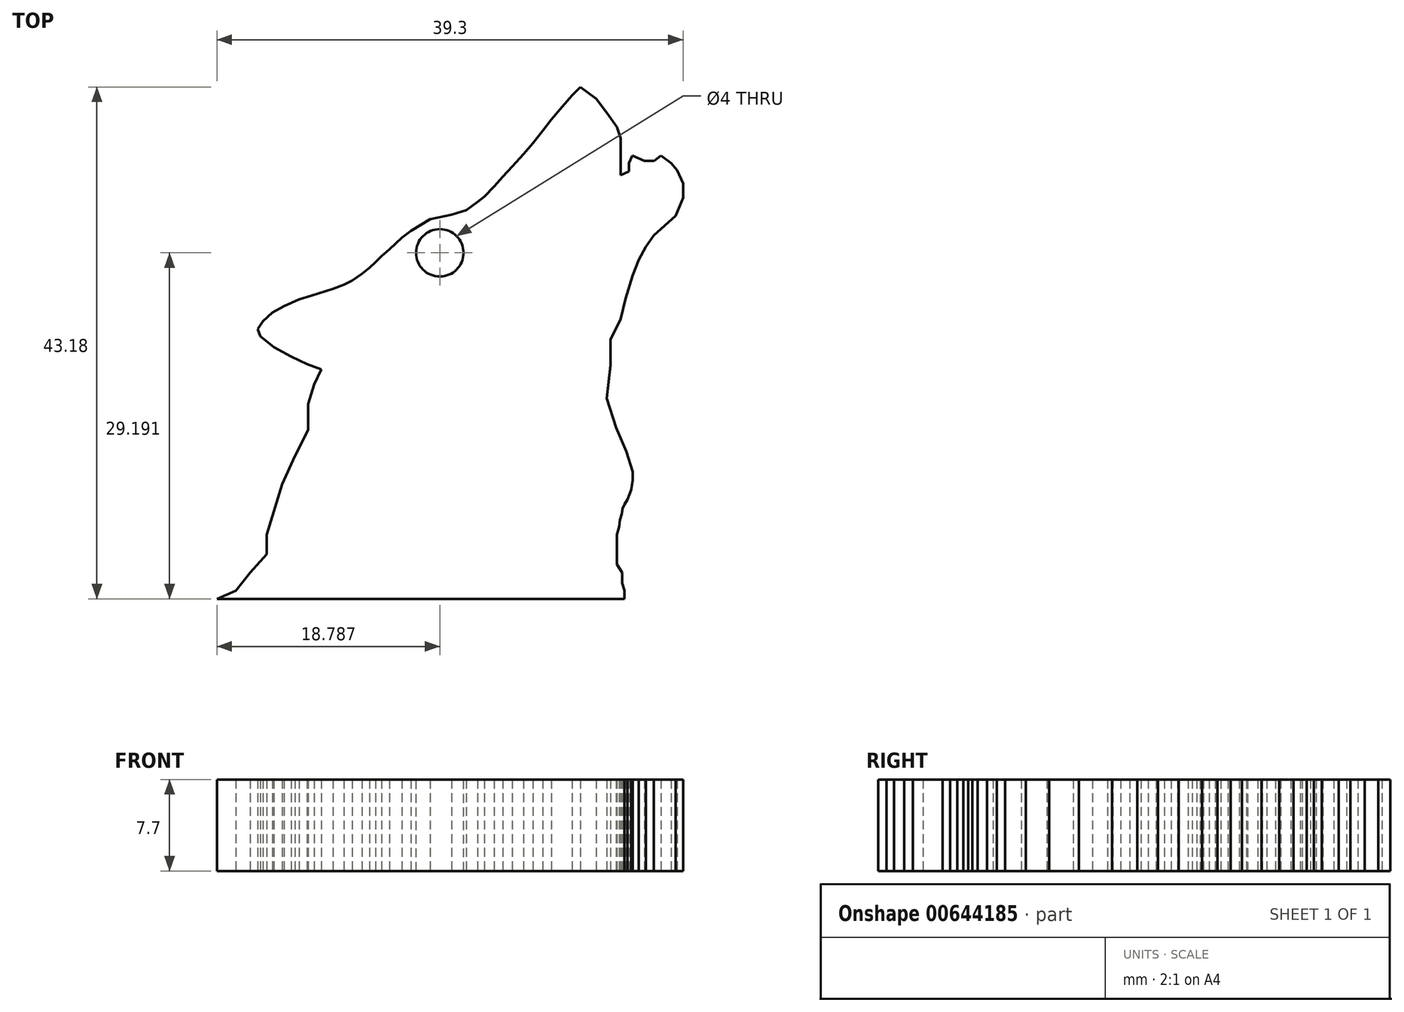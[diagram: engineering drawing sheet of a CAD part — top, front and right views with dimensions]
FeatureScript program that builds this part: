
annotation { "Feature Type Name" : "Feature", "Feature Type Description" : "" }
export const myFeature = defineFeature(function(context is Context, id is Id, definition is map)
    precondition{}
    {
        {
            var Q0;
            Q0=qCreatedBy(makeId("Top.planeOp"),FACE);
            var sketch = newSketch(context, id + "F0", { "sketchPlane" : qUnion([Q0])});
            skLineSegment(sketch, "E0", {"start": v(-37.66, 39.45) * mm, "end": v(-38.87, 39.9) * mm});
            skLineSegment(sketch, "E1", {"start": v(-38.87, 39.9) * mm, "end": v(-40.2, 40.55) * mm});
            skLineSegment(sketch, "E2", {"start": v(-40.2, 40.55) * mm, "end": v(-41.64, 41.33) * mm});
            skLineSegment(sketch, "E3", {"start": v(-41.64, 41.33) * mm, "end": v(-42.8, 42.26) * mm});
            skLineSegment(sketch, "E4", {"start": v(-42.8, 42.26) * mm, "end": v(-43.02, 42.87) * mm});
            skLineSegment(sketch, "E5", {"start": v(-43.02, 42.87) * mm, "end": v(-42.58, 43.53) * mm});
            skLineSegment(sketch, "E6", {"start": v(-42.58, 43.53) * mm, "end": v(-41.77, 44.24) * mm});
            skLineSegment(sketch, "E7", {"start": v(-41.77, 44.24) * mm, "end": v(-40.79, 44.8) * mm});
            skLineSegment(sketch, "E8", {"start": v(-40.79, 44.8) * mm, "end": v(-39.53, 45.35) * mm});
            skLineSegment(sketch, "E9", {"start": v(-39.53, 45.35) * mm, "end": v(-38.46, 45.68) * mm});
            skLineSegment(sketch, "E10", {"start": v(-38.46, 45.68) * mm, "end": v(-36.68, 46.24) * mm});
            skLineSegment(sketch, "E11", {"start": v(-36.68, 46.24) * mm, "end": v(-35.74, 46.6) * mm});
            skLineSegment(sketch, "E12", {"start": v(-35.74, 46.6) * mm, "end": v(-35.04, 46.96) * mm});
            skLineSegment(sketch, "E13", {"start": v(-35.04, 46.96) * mm, "end": v(-34.22, 47.52) * mm});
            skLineSegment(sketch, "E14", {"start": v(-34.22, 47.52) * mm, "end": v(-33.6, 48.02) * mm});
            skLineSegment(sketch, "E15", {"start": v(-33.6, 48.02) * mm, "end": v(-33.08, 48.52) * mm});
            skLineSegment(sketch, "E16", {"start": v(-33.08, 48.52) * mm, "end": v(-32.58, 49.01) * mm});
            skLineSegment(sketch, "E17", {"start": v(-32.58, 49.01) * mm, "end": v(-31.92, 49.6) * mm});
            skLineSegment(sketch, "E18", {"start": v(-31.92, 49.6) * mm, "end": v(-31.4, 50.06) * mm});
            skLineSegment(sketch, "E19", {"start": v(-31.4, 50.06) * mm, "end": v(-30.86, 50.57) * mm});
            skLineSegment(sketch, "E20", {"start": v(-30.86, 50.57) * mm, "end": v(-30.1, 51.15) * mm});
            skLineSegment(sketch, "E21", {"start": v(-30.1, 51.15) * mm, "end": v(-28.46, 52.13) * mm});
            skLineSegment(sketch, "E22", {"start": v(-28.46, 52.13) * mm, "end": v(-26.65, 52.5) * mm});
            skLineSegment(sketch, "E23", {"start": v(-26.65, 52.5) * mm, "end": v(-25.42, 52.89) * mm});
            skLineSegment(sketch, "E24", {"start": v(-25.42, 52.89) * mm, "end": v(-24.47, 53.59) * mm});
            skLineSegment(sketch, "E25", {"start": v(-24.47, 53.59) * mm, "end": v(-23.9, 54.05) * mm});
            skLineSegment(sketch, "E26", {"start": v(-23.9, 54.05) * mm, "end": v(-23.08, 54.9) * mm});
            skLineSegment(sketch, "E27", {"start": v(-23.08, 54.9) * mm, "end": v(-22.33, 55.7) * mm});
            skLineSegment(sketch, "E28", {"start": v(-22.33, 55.7) * mm, "end": v(-21.57, 56.56) * mm});
            skLineSegment(sketch, "E29", {"start": v(-21.57, 56.56) * mm, "end": v(-20.59, 57.61) * mm});
            skLineSegment(sketch, "E30", {"start": v(-20.59, 57.61) * mm, "end": v(-19.8, 58.54) * mm});
            skLineSegment(sketch, "E31", {"start": v(-19.8, 58.54) * mm, "end": v(-19, 59.6) * mm});
            skLineSegment(sketch, "E32", {"start": v(-19, 59.6) * mm, "end": v(-18.25, 60.54) * mm});
            skLineSegment(sketch, "E33", {"start": v(-18.25, 60.54) * mm, "end": v(-17.32, 61.62) * mm});
            skLineSegment(sketch, "E34", {"start": v(-17.32, 61.62) * mm, "end": v(-16.5, 62.58) * mm});
            skLineSegment(sketch, "E35", {"start": v(-16.5, 62.58) * mm, "end": v(-15.8, 63.28) * mm});
            skLineSegment(sketch, "E36", {"start": v(-15.8, 63.28) * mm, "end": v(-14.5, 62.27) * mm});
            skLineSegment(sketch, "E37", {"start": v(-14.5, 62.27) * mm, "end": v(-13.58, 61.13) * mm});
            skLineSegment(sketch, "E38", {"start": v(-13.58, 61.13) * mm, "end": v(-12.71, 59.91) * mm});
            skLineSegment(sketch, "E39", {"start": v(-12.71, 59.91) * mm, "end": v(-12.41, 58.95) * mm});
            skLineSegment(sketch, "E40", {"start": v(-12.41, 58.95) * mm, "end": v(-12.41, 57.55) * mm});
            skLineSegment(sketch, "E41", {"start": v(-12.41, 57.55) * mm, "end": v(-12.41, 55.85) * mm});
            skLineSegment(sketch, "E42", {"start": v(-12.41, 55.85) * mm, "end": v(-11.7, 56.16) * mm});
            skLineSegment(sketch, "E43", {"start": v(-11.7, 56.16) * mm, "end": v(-11.7, 56.85) * mm});
            skLineSegment(sketch, "E44", {"start": v(-11.7, 56.85) * mm, "end": v(-11.43, 57.48) * mm});
            skLineSegment(sketch, "E45", {"start": v(-11.43, 57.48) * mm, "end": v(-10.42, 57.05) * mm});
            skLineSegment(sketch, "E46", {"start": v(-10.42, 57.05) * mm, "end": v(-9.58, 57.05) * mm});
            skLineSegment(sketch, "E47", {"start": v(-9.58, 57.05) * mm, "end": v(-9.02, 57.5) * mm});
            skLineSegment(sketch, "E48", {"start": v(-9.02, 57.5) * mm, "end": v(-8.16, 56.85) * mm});
            skLineSegment(sketch, "E49", {"start": v(-8.16, 56.85) * mm, "end": v(-7.64, 56.25) * mm});
            skLineSegment(sketch, "E50", {"start": v(-7.64, 56.25) * mm, "end": v(-7.15, 55.14) * mm});
            skLineSegment(sketch, "E51", {"start": v(-7.15, 55.14) * mm, "end": v(-7.15, 53.93) * mm});
            skLineSegment(sketch, "E52", {"start": v(-7.15, 53.93) * mm, "end": v(-7.76, 52.41) * mm});
            skLineSegment(sketch, "E53", {"start": v(-7.76, 52.41) * mm, "end": v(-9.63, 50.78) * mm});
            skLineSegment(sketch, "E54", {"start": v(-9.63, 50.78) * mm, "end": v(-10.28, 49.83) * mm});
            skLineSegment(sketch, "E55", {"start": v(-10.28, 49.83) * mm, "end": v(-10.87, 48.71) * mm});
            skLineSegment(sketch, "E56", {"start": v(-10.87, 48.71) * mm, "end": v(-11.4, 47.4) * mm});
            skLineSegment(sketch, "E57", {"start": v(-11.4, 47.4) * mm, "end": v(-11.99, 45.44) * mm});
            skLineSegment(sketch, "E58", {"start": v(-11.99, 45.44) * mm, "end": v(-12.41, 43.71) * mm});
            skLineSegment(sketch, "E59", {"start": v(-12.41, 43.71) * mm, "end": v(-13.28, 41.95) * mm});
            skLineSegment(sketch, "E60", {"start": v(-13.28, 41.95) * mm, "end": v(-13.28, 39.82) * mm});
            skLineSegment(sketch, "E61", {"start": v(-13.28, 39.82) * mm, "end": v(-13.58, 37.03) * mm});
            skLineSegment(sketch, "E62", {"start": v(-13.58, 37.03) * mm, "end": v(-13.28, 36.06) * mm});
            skLineSegment(sketch, "E63", {"start": v(-13.28, 36.06) * mm, "end": v(-12.8, 34.53) * mm});
            skLineSegment(sketch, "E64", {"start": v(-12.8, 34.53) * mm, "end": v(-11.93, 32.55) * mm});
            skLineSegment(sketch, "E65", {"start": v(-11.93, 32.55) * mm, "end": v(-11.38, 30.81) * mm});
            skLineSegment(sketch, "E66", {"start": v(-11.38, 30.81) * mm, "end": v(-11.38, 30.12) * mm});
            skLineSegment(sketch, "E67", {"start": v(-11.38, 30.12) * mm, "end": v(-11.53, 29.3) * mm});
            skLineSegment(sketch, "E68", {"start": v(-11.53, 29.3) * mm, "end": v(-11.85, 28.48) * mm});
            skLineSegment(sketch, "E69", {"start": v(-11.85, 28.48) * mm, "end": v(-12.09, 28.06) * mm});
            skLineSegment(sketch, "E70", {"start": v(-12.09, 28.06) * mm, "end": v(-12.25, 27.7) * mm});
            skLineSegment(sketch, "E71", {"start": v(-12.25, 27.7) * mm, "end": v(-12.32, 27.28) * mm});
            skLineSegment(sketch, "E72", {"start": v(-12.32, 27.28) * mm, "end": v(-12.48, 26.77) * mm});
            skLineSegment(sketch, "E73", {"start": v(-12.48, 26.77) * mm, "end": v(-12.53, 26.18) * mm});
            skLineSegment(sketch, "E74", {"start": v(-12.53, 26.18) * mm, "end": v(-12.73, 25.52) * mm});
            skLineSegment(sketch, "E75", {"start": v(-12.73, 25.52) * mm, "end": v(-12.73, 24.66) * mm});
            skLineSegment(sketch, "E76", {"start": v(-12.73, 24.66) * mm, "end": v(-12.73, 23.8) * mm});
            skLineSegment(sketch, "E77", {"start": v(-12.73, 23.8) * mm, "end": v(-12.73, 23.01) * mm});
            skLineSegment(sketch, "E78", {"start": v(-12.73, 23.01) * mm, "end": v(-12.29, 22.3) * mm});
            skLineSegment(sketch, "E79", {"start": v(-12.29, 22.3) * mm, "end": v(-12.29, 21.44) * mm});
            skLineSegment(sketch, "E80", {"start": v(-12.29, 21.44) * mm, "end": v(-12.09, 20.8) * mm});
            skLineSegment(sketch, "E81", {"start": v(-12.09, 20.8) * mm, "end": v(-12.09, 20.1) * mm});
            skLineSegment(sketch, "E82", {"start": v(-12.09, 20.1) * mm, "end": v(-46.45, 20.1) * mm});
            skLineSegment(sketch, "E83", {"start": v(-46.45, 20.1) * mm, "end": v(-44.87, 20.8) * mm});
            skLineSegment(sketch, "E84", {"start": v(-44.87, 20.8) * mm, "end": v(-43.66, 22.3) * mm});
            skLineSegment(sketch, "E85", {"start": v(-43.66, 22.3) * mm, "end": v(-42.25, 23.88) * mm});
            skLineSegment(sketch, "E86", {"start": v(-42.25, 23.88) * mm, "end": v(-42.25, 25.5) * mm});
            skLineSegment(sketch, "E87", {"start": v(-42.25, 25.5) * mm, "end": v(-41.67, 27.4) * mm});
            skLineSegment(sketch, "E88", {"start": v(-41.67, 27.4) * mm, "end": v(-40.95, 29.79) * mm});
            skLineSegment(sketch, "E89", {"start": v(-40.95, 29.79) * mm, "end": v(-39.87, 32.17) * mm});
            skLineSegment(sketch, "E90", {"start": v(-39.87, 32.17) * mm, "end": v(-38.75, 34.33) * mm});
            skLineSegment(sketch, "E91", {"start": v(-38.75, 34.33) * mm, "end": v(-38.75, 36.54) * mm});
            skLineSegment(sketch, "E92", {"start": v(-38.75, 36.54) * mm, "end": v(-38.25, 38.19) * mm});
            skLineSegment(sketch, "E93", {"start": v(-38.25, 38.19) * mm, "end": v(-37.66, 39.45) * mm});
            skSolve(sketch);
        }
        {
            var Q0;
            Q0 = qSketchRegion(id + "F0", true);
            extrude(context, id + "F1", {"entities" : qUnion([Q0]), "depth" : 7.7 * mm, "offsetDistance" : 25.4 * mm});
        }
        {
            var Q0;
            Q0=makeQuery(id+"F1.opExtrude","CAP_FACE",FACE,{"disambiguationData":[OSD([sQuery(id+"F0.wireOp",EDGE,"E0"),sQuery(id+"F0.wireOp",EDGE,"E1"),sQuery(id+"F0.wireOp",EDGE,"E2"),sQuery(id+"F0.wireOp",EDGE,"E3"),sQuery(id+"F0.wireOp",EDGE,"E4"),sQuery(id+"F0.wireOp",EDGE,"E5"),sQuery(id+"F0.wireOp",EDGE,"E6"),sQuery(id+"F0.wireOp",EDGE,"E7"),sQuery(id+"F0.wireOp",EDGE,"E8"),sQuery(id+"F0.wireOp",EDGE,"E9"),sQuery(id+"F0.wireOp",EDGE,"E10"),sQuery(id+"F0.wireOp",EDGE,"E11"),sQuery(id+"F0.wireOp",EDGE,"E12"),sQuery(id+"F0.wireOp",EDGE,"E13"),sQuery(id+"F0.wireOp",EDGE,"E14"),sQuery(id+"F0.wireOp",EDGE,"E15"),sQuery(id+"F0.wireOp",EDGE,"E16"),sQuery(id+"F0.wireOp",EDGE,"E17"),sQuery(id+"F0.wireOp",EDGE,"E18"),sQuery(id+"F0.wireOp",EDGE,"E19"),sQuery(id+"F0.wireOp",EDGE,"E20"),sQuery(id+"F0.wireOp",EDGE,"E21"),sQuery(id+"F0.wireOp",EDGE,"E22"),sQuery(id+"F0.wireOp",EDGE,"E23"),sQuery(id+"F0.wireOp",EDGE,"E24"),sQuery(id+"F0.wireOp",EDGE,"E25"),sQuery(id+"F0.wireOp",EDGE,"E26"),sQuery(id+"F0.wireOp",EDGE,"E27"),sQuery(id+"F0.wireOp",EDGE,"E28"),sQuery(id+"F0.wireOp",EDGE,"E29"),sQuery(id+"F0.wireOp",EDGE,"E30"),sQuery(id+"F0.wireOp",EDGE,"E31"),sQuery(id+"F0.wireOp",EDGE,"E32"),sQuery(id+"F0.wireOp",EDGE,"E33"),sQuery(id+"F0.wireOp",EDGE,"E34"),sQuery(id+"F0.wireOp",EDGE,"E35"),sQuery(id+"F0.wireOp",EDGE,"E36"),sQuery(id+"F0.wireOp",EDGE,"E37"),sQuery(id+"F0.wireOp",EDGE,"E38"),sQuery(id+"F0.wireOp",EDGE,"E39"),sQuery(id+"F0.wireOp",EDGE,"E40"),sQuery(id+"F0.wireOp",EDGE,"E41"),sQuery(id+"F0.wireOp",EDGE,"E42"),sQuery(id+"F0.wireOp",EDGE,"E43"),sQuery(id+"F0.wireOp",EDGE,"E44"),sQuery(id+"F0.wireOp",EDGE,"E45"),sQuery(id+"F0.wireOp",EDGE,"E46"),sQuery(id+"F0.wireOp",EDGE,"E47"),sQuery(id+"F0.wireOp",EDGE,"E48"),sQuery(id+"F0.wireOp",EDGE,"E49"),sQuery(id+"F0.wireOp",EDGE,"E50"),sQuery(id+"F0.wireOp",EDGE,"E51"),sQuery(id+"F0.wireOp",EDGE,"E52"),sQuery(id+"F0.wireOp",EDGE,"E53"),sQuery(id+"F0.wireOp",EDGE,"E54"),sQuery(id+"F0.wireOp",EDGE,"E55"),sQuery(id+"F0.wireOp",EDGE,"E56"),sQuery(id+"F0.wireOp",EDGE,"E57"),sQuery(id+"F0.wireOp",EDGE,"E58"),sQuery(id+"F0.wireOp",EDGE,"E59"),sQuery(id+"F0.wireOp",EDGE,"E60"),sQuery(id+"F0.wireOp",EDGE,"E61"),sQuery(id+"F0.wireOp",EDGE,"E62"),sQuery(id+"F0.wireOp",EDGE,"E63"),sQuery(id+"F0.wireOp",EDGE,"E64"),sQuery(id+"F0.wireOp",EDGE,"E65"),sQuery(id+"F0.wireOp",EDGE,"E66"),sQuery(id+"F0.wireOp",EDGE,"E67"),sQuery(id+"F0.wireOp",EDGE,"E68"),sQuery(id+"F0.wireOp",EDGE,"E69"),sQuery(id+"F0.wireOp",EDGE,"E70"),sQuery(id+"F0.wireOp",EDGE,"E71"),sQuery(id+"F0.wireOp",EDGE,"E72"),sQuery(id+"F0.wireOp",EDGE,"E73"),sQuery(id+"F0.wireOp",EDGE,"E74"),sQuery(id+"F0.wireOp",EDGE,"E75"),sQuery(id+"F0.wireOp",EDGE,"E76"),sQuery(id+"F0.wireOp",EDGE,"E77"),sQuery(id+"F0.wireOp",EDGE,"E78"),sQuery(id+"F0.wireOp",EDGE,"E79"),sQuery(id+"F0.wireOp",EDGE,"E80"),sQuery(id+"F0.wireOp",EDGE,"E81"),sQuery(id+"F0.wireOp",EDGE,"E82"),sQuery(id+"F0.wireOp",EDGE,"E83"),sQuery(id+"F0.wireOp",EDGE,"E84"),sQuery(id+"F0.wireOp",EDGE,"E85"),sQuery(id+"F0.wireOp",EDGE,"E86"),sQuery(id+"F0.wireOp",EDGE,"E87"),sQuery(id+"F0.wireOp",EDGE,"E88"),sQuery(id+"F0.wireOp",EDGE,"E89"),sQuery(id+"F0.wireOp",EDGE,"E90"),sQuery(id+"F0.wireOp",EDGE,"E91"),sQuery(id+"F0.wireOp",EDGE,"E92"),sQuery(id+"F0.wireOp",EDGE,"E93")])],"isStart":false});
            var sketch = newSketch(context, id + "F2", { "sketchPlane" : qUnion([Q0])});
            skCircle(sketch, "E94", {"center": v(-27.66, 49.3) * mm, "radius": 2 * mm});
            skSolve(sketch);
        }
        {
            var Q0;
            Q0 = qSketchRegion(id + "F2", true);
            extrude(context, id + "F3", {"entities" : qUnion([Q0]), "operationType" : NewBodyOperationType.REMOVE, "oppositeDirection" : true, "depth" : 14.4 * mm, "offsetDistance" : 25 * mm});
        }
    });
